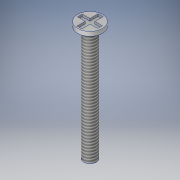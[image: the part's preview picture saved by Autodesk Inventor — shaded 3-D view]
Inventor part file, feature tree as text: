
AUTODESK INVENTOR PART (.ipt)
format: ipt  version: 2018 (Build 220112000, 112)  size: 126,976 bytes
history: native  units: in
note: dims shown in document units (in); Inventor stores cm internally (conversion verified against a paired STEP export)
features: sketch x2, revolve x1, thread x1, extrude x1
ambient origin geometry x8: Origin, YZ Plane, XZ Plane, XY Plane, X Axis, Y Axis, Z Axis, Center Point
bodies: Solid1 (feature_tree)
feature tree (5):
  revolve  "Revolution1"  [1 undecoded]
  thread  "Thread1"  [1 undecoded]
  extrude  "Extrusion1"  TaperAngle=90.0deg  [1 undecoded]
  sketch  "Sketch1"  dims[d0=0.07in d1=0.024in d2=0.0345in]
  sketch  "Sketch2"  dims[d3=0.65in d4=90.0deg d5=90.0deg d6=90.0deg d7=1.0in d8=0.0in d9=0.0125in d10=0.0in]
note: 3 required parameter values undecoded (feature->parameter linkage not recoverable at this tier; creation-order binding heuristic only, values carry confidence <= 0.55)